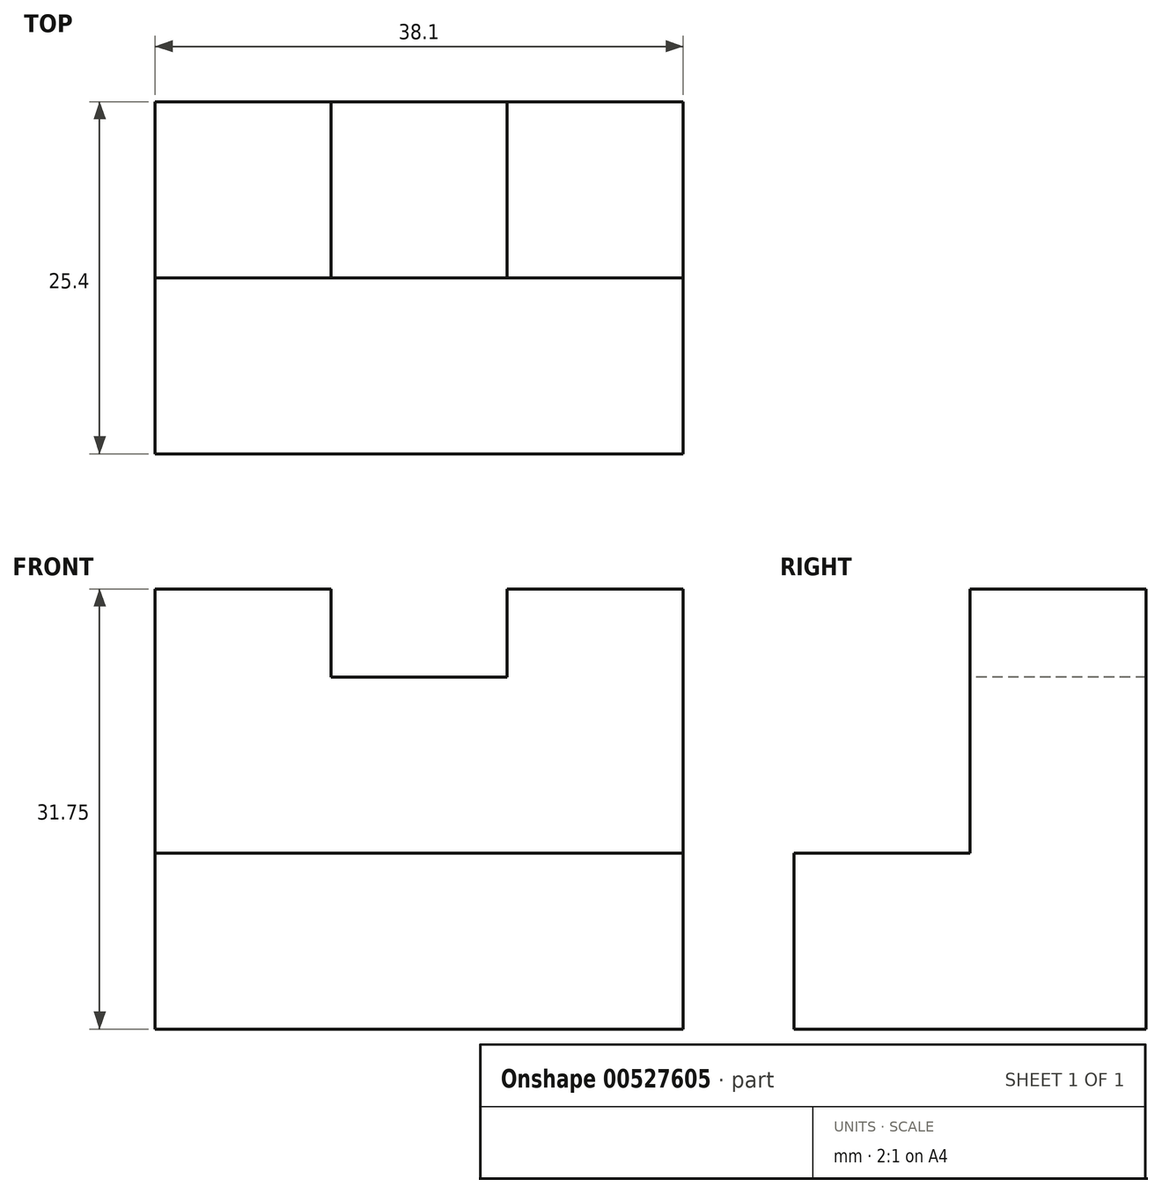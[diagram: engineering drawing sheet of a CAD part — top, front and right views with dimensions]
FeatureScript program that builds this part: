
annotation { "Feature Type Name" : "Feature", "Feature Type Description" : "" }
export const myFeature = defineFeature(function(context is Context, id is Id, definition is map)
    precondition{}
    {
        {
            var Q0;
            Q0=qCreatedBy(makeId("Right.planeOp"),FACE);
            var sketch = newSketch(context, id + "F0", { "sketchPlane" : qUnion([Q0])});
            skLineSegment(sketch, "E0", {"start": v(1.56, 0) * mm, "end": v(0, 0) * mm});
            skLineSegment(sketch, "E1", {"start": v(0, 0) * mm, "end": v(25.4, 0) * mm});
            skLineSegment(sketch, "E2", {"start": v(25.4, 0) * mm, "end": v(25.4, 31.75) * mm});
            skLineSegment(sketch, "E3", {"start": v(25.4, 31.75) * mm, "end": v(12.7, 31.75) * mm});
            skLineSegment(sketch, "E4", {"start": v(12.7, 31.75) * mm, "end": v(12.7, 12.7) * mm});
            skLineSegment(sketch, "E5", {"start": v(12.7, 12.7) * mm, "end": v(0, 12.7) * mm});
            skLineSegment(sketch, "E6", {"start": v(0, 12.7) * mm, "end": v(0, 0) * mm});
            skSolve(sketch);
        }
        {
            var Q0;
            {var subQ0=sQuery(id+"F0.wireOp",EDGE,"E2");Q0=makeQuery(id+"F0.imprint","IMPRINT",FACE,{"disambiguationData":[TD([[makeQuery(id+"F0.imprint","IMPRINT",EDGE,{"derivedFrom":subQ0}),1.0]])]});}
            extrude(context, id + "F1", {"entities" : qUnion([Q0]), "depth" : 38.1 * mm, "offsetDistance" : 25.4 * mm});
        }
        {
            var Q0;
            Q0=makeQuery(id+"F1.opExtrude","SWEPT_FACE",FACE,{"disambiguationData":[OSD([sQuery(id+"F0.wireOp",EDGE,"E3")])]});
            var sketch = newSketch(context, id + "F2", { "sketchPlane" : qUnion([Q0])});
            skLineSegment(sketch, "E7", {"start": v(12.7, 25.4) * mm, "end": v(12.7, 12.7) * mm});
            skPoint(sketch, "E7.endSnap0", {"position": v(19.05, 12.7) * mm});
            skLineSegment(sketch, "E8", {"start": v(12.7, 12.7) * mm, "end": v(25.4, 12.7) * mm});
            skLineSegment(sketch, "E9", {"start": v(25.4, 12.7) * mm, "end": v(25.4, 25.4) * mm});
            skLineSegment(sketch, "E10", {"start": v(25.4, 25.4) * mm, "end": v(12.7, 25.4) * mm});
            skSolve(sketch);
        }
        {
            var Q0;
            Q0 = qSketchRegion(id + "F2", true);
            extrude(context, id + "F3", {"entities" : qUnion([Q0]), "operationType" : NewBodyOperationType.REMOVE, "oppositeDirection" : true, "depth" : 6.35 * mm, "offsetDistance" : 25.4 * mm});
        }
    });
